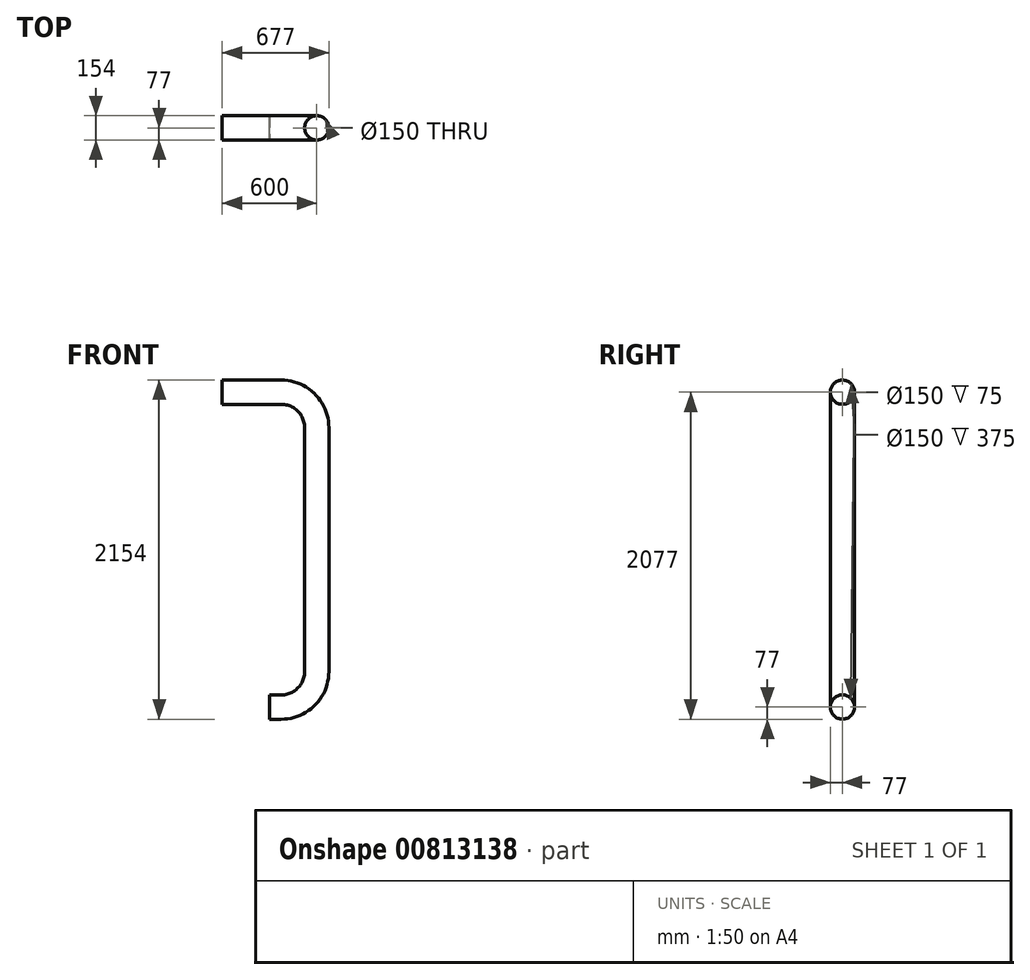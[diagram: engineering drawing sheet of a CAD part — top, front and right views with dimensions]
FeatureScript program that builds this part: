
annotation { "Feature Type Name" : "Feature", "Feature Type Description" : "" }
export const myFeature = defineFeature(function(context is Context, id is Id, definition is map)
    precondition{}
    {
        {
            var Q0;
            Q0=qCreatedBy(makeId("Right.planeOp"),FACE);
            var sketch = newSketch(context, id + "F0", { "sketchPlane" : qUnion([Q0])});
            skCircle(sketch, "E0", {"center": v(0, 0) * mm, "radius": 77 * mm});
            skCircle(sketch, "E1", {"center": v(0, 0) * mm, "radius": 75 * mm});
            skSolve(sketch);
        }
        {
            var Q0;
            Q0=qCreatedBy(makeId("Front.planeOp"),FACE);
            var sketch = newSketch(context, id + "F1", { "sketchPlane" : qUnion([Q0])});
            skLineSegment(sketch, "E2", {"start": v(0, 0) * mm, "end": v(375, 0) * mm});
            skLineSegment(sketch, "E3", {"start": v(600, -225) * mm, "end": v(600, -1775) * mm});
            skLineSegment(sketch, "E4", {"start": v(375, -2000) * mm, "end": v(300, -2000) * mm});
            skPoint(sketch, "E5.visualSharp", {"position": v(600, 0) * mm});
            skArc(sketch, "E5.filletArc", {"start": v(600, -225) * mm, "mid": v(534.1, -65.9) * mm, "end": v(375, 0) * mm});
            skPoint(sketch, "E6.visualSharp", {"position": v(600, -2000) * mm});
            skArc(sketch, "E6.filletArc", {"start": v(375, -2000) * mm, "mid": v(534.1, -1934.1) * mm, "end": v(600, -1775) * mm});
            skSolve(sketch);
        }
        {
            var Q0;
            Q0=makeQuery(id+"F0.imprint","IMPRINT",FACE,{"disambiguationData":[TD([[makeQuery(id+"F0.imprint","IMPRINT",EDGE,{"derivedFrom":sQuery(id+"F0.wireOp",EDGE,"E0")}),1.0]])]});
            var Q1;
            Q1=sQuery(id+"F1.wireOp",EDGE,"E2");
            var Q2;
            Q2=sQuery(id+"F1.wireOp",EDGE,"E5.filletArc");
            var Q3;
            Q3=sQuery(id+"F1.wireOp",EDGE,"E3");
            var Q4;
            Q4=sQuery(id+"F1.wireOp",EDGE,"E6.filletArc");
            var Q5;
            Q5=sQuery(id+"F1.wireOp",EDGE,"E4");
            sweep(context, id + "F2", {"profiles" : qUnion([Q0]), "path" : qUnion([Q1, Q2, Q3, Q4, Q5])});
        }
    });
